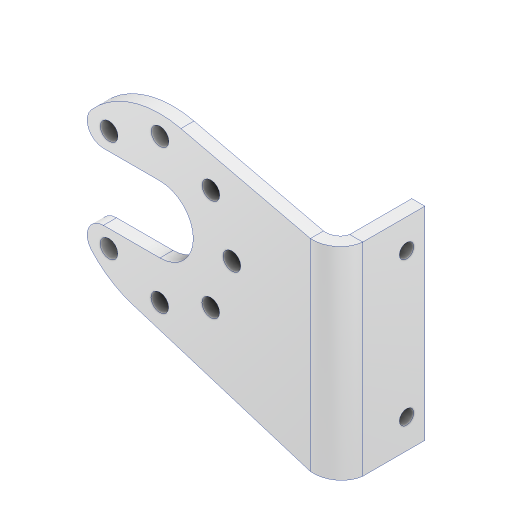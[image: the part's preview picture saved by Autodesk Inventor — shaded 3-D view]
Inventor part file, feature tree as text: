
AUTODESK INVENTOR PART (.ipt)
format: ipt  version: 2023.2 (Build 272271000, 271)  size: 251,904 bytes
history: native  units: mm
features: other x5, sketch x3, extrude x2, fillet x1
ambient origin geometry x8: Origin, YZ Plane, XZ Plane, XY Plane, X Axis, Y Axis, Z Axis, Center Point
bodies: Body1 (feature_tree)
feature tree (11):
  other  "솔리드1"
  extrude  "돌출1"  Depth=10.2mm
  other  "플랜지1"
  extrude  "돌출2"  Depth=2.0mm TaperAngle=0.0deg
  fillet  "모깎기2"  Radius=2.0mm
  sketch  "스케치1"
  sketch  "스케치2"
  other  "절곡부1"
  other  "구석1"
  sketch  "스케치3"
  other  "정의1"
